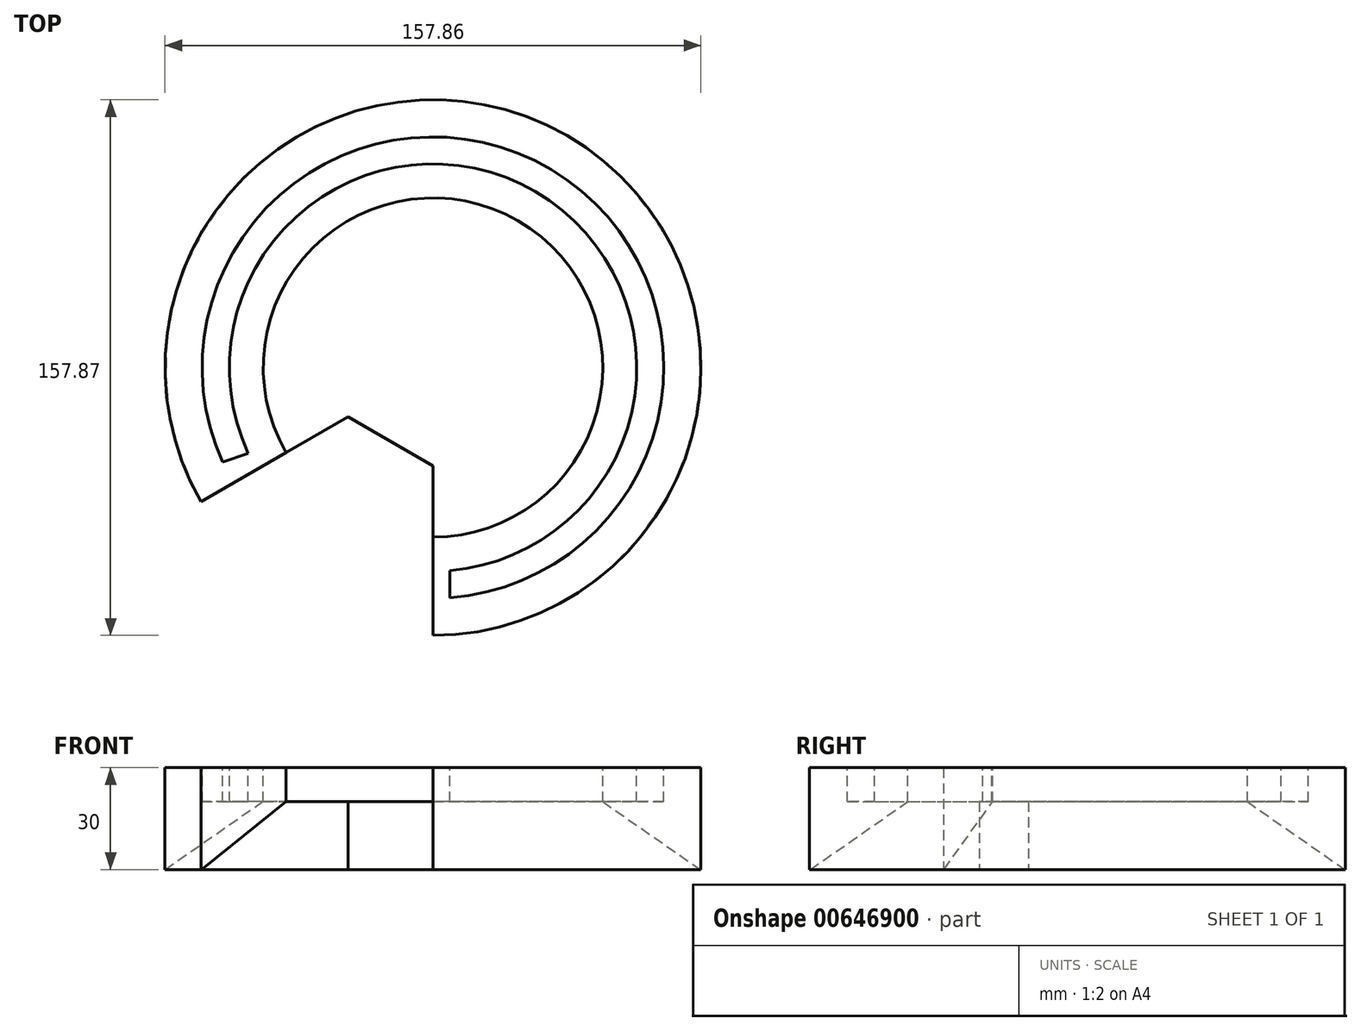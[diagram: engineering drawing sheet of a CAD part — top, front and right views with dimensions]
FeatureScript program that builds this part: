
annotation { "Feature Type Name" : "Feature", "Feature Type Description" : "" }
export const myFeature = defineFeature(function(context is Context, id is Id, definition is map)
    precondition{}
    {
        {
            var Q0;
            Q0=qCreatedBy(makeId("Right.planeOp"),FACE);
            var sketch = newSketch(context, id + "F0", { "sketchPlane" : qUnion([Q0])});
            skLineSegment(sketch, "E0", {"start": v(-117.4, 26.08) * mm, "end": v(-117.4, 6.08) * mm});
            skLineSegment(sketch, "E1", {"start": v(-117.4, 6.08) * mm, "end": v(-196.12, 6.08) * mm});
            skLineSegment(sketch, "E2", {"start": v(-196.12, 6.08) * mm, "end": v(-167.4, 26.08) * mm});
            skLineSegment(sketch, "E3", {"start": v(-167.4, 26.08) * mm, "end": v(-117.4, 26.08) * mm});
            skSolve(sketch);
        }
        {
            var Q0;
            Q0=makeQuery(id+"F0.imprint","IMPRINT",FACE,{"disambiguationData":[TD([[makeQuery(id+"F0.imprint","IMPRINT",EDGE,{"derivedFrom":sQuery(id+"F0.wireOp",EDGE,"E0")}),-1.0]])]});
            var Q1;
            Q1=sQuery(id+"F0.wireOp",EDGE,"E0");
            revolve(context, id + "F1", {"surfaceOperationType" : NewSurfaceOperationType.NEW, "entities" : qUnion([Q0]), "axis" : qUnion([Q1]), "revolveType" : RevolveType.FULL});
        }
        {
            var Q0;
            Q0=makeQuery(id+"F1.opRevolve","SWEPT_FACE",FACE,{"disambiguationData":[OSD([sQuery(id+"F0.wireOp",EDGE,"E1")])]});
            var sketch = newSketch(context, id + "F2", { "sketchPlane" : qUnion([Q0])});
            skCircle(sketch, "E4", {"center": v(0, 117.4) * mm, "radius": 78.93 * mm});
            skSolve(sketch);
        }
        {
            var Q0;
            Q0 = qSketchRegion(id + "F2", true);
            extrude(context, id + "F3", {"entities" : qUnion([Q0]), "oppositeDirection" : true, "depth" : 30 * mm, "offsetDistance" : 25 * mm});
        }
        {
            var Q0;
            Q0=makeQuery(id+"F3.opExtrude","CAP_FACE",FACE,{"disambiguationData":[OSD([sQuery(id+"F2.wireOp",EDGE,"E4")])],"isStart":true});
            var sketch = newSketch(context, id + "F4", { "sketchPlane" : qUnion([Q0])});
            skArc(sketch, "E5", {"start": v(-68.36, 156.87) * mm, "mid": v(-39.47, 185.76) * mm, "end": v(0, 196.34) * mm});
            skLineSegment(sketch, "E6", {"start": v(-68.36, 156.87) * mm, "end": v(-25.06, 131.87) * mm});
            skLineSegment(sketch, "E7", {"start": v(0, 196.34) * mm, "end": v(0, 146.34) * mm});
            skLineSegment(sketch, "E8", {"start": v(-25.06, 131.87) * mm, "end": v(0, 146.34) * mm});
            skSolve(sketch);
        }
        {
            var Q0;
            Q0 = qSketchRegion(id + "F4", true);
            extrude(context, id + "F5", {"entities" : qUnion([Q0]), "operationType" : NewBodyOperationType.REMOVE, "oppositeDirection" : true, "depth" : 30 * mm, "offsetDistance" : 25 * mm});
        }
        {
            var Q0;
            Q0=makeQuery(id+"F3.opExtrude","CAP_FACE",FACE,{"disambiguationData":[OSD([sQuery(id+"F2.wireOp",EDGE,"E4")])],"isStart":false});
            var sketch = newSketch(context, id + "F6", { "sketchPlane" : qUnion([Q0])});
            skCircle(sketch, "E9", {"center": v(0, -117.4) * mm, "radius": 67.98 * mm});
            skCircle(sketch, "E10", {"center": v(0, -117.4) * mm, "radius": 60 * mm});
            skLineSegment(sketch, "E11", {"start": v(-62, -145.3) * mm, "end": v(-54.43, -142.65) * mm});
            skLineSegment(sketch, "E12", {"start": v(4.99, -177.2) * mm, "end": v(4.99, -185.2) * mm});
            skCircle(sketch, "E13", {"center": v(0, -117.4) * mm, "radius": 50 * mm});
            skSolve(sketch);
        }
        {
            var Q0;
            {var subQ5=sQuery(id+"F6.wireOp",EDGE,"E11");Q0=makeQuery(id+"F6.imprint","IMPRINT",FACE,{"disambiguationData":[TD([[makeQuery(id+"F6.imprint","IMPRINT",EDGE,{"derivedFrom":subQ5}),1.0]])]});}
            extrude(context, id + "F7", {"entities" : qUnion([Q0]), "operationType" : NewBodyOperationType.REMOVE, "oppositeDirection" : true, "depth" : 10 * mm, "offsetDistance" : 25 * mm});
        }
        {
            var Q0;
            Q0=makeQuery(id+"F6.imprint","IMPRINT",FACE,{"disambiguationData":[TD([[makeQuery(id+"F6.imprint","IMPRINT",EDGE,{"derivedFrom":sQuery(id+"F6.wireOp",EDGE,"E13")}),1.0]])]});
            extrude(context, id + "F8", {"entities" : qUnion([Q0]), "operationType" : NewBodyOperationType.REMOVE, "oppositeDirection" : true, "depth" : 10 * mm, "offsetDistance" : 25 * mm});
        }
    });
